# Revit family: ВЦН_ЕС_Eng
name_source: partatom
category: Mechanical Equipment
units: mm (PartAtom-declared; Revit-internal decimal feet)

## family parameters
Always vertical = Yes
Classification = None
Cut with Voids When Loaded = No
Part Type = Normal
Room Calculation Point = No
Round Connector Dimension = Use Diameter
Shared = No
Work Plane-Based = No

## types (16) — shared parameters
00_20_Manufacturer = Vents
00_20_Name = Exhaust centrifugal fan
Casing Material = Metal, painted, blue, matte RAL 5007
Description = External wall mounting
Frequency = 50 Hz
Load Classification = HVAC
Maintenance zone material = <By Category>
Manufacturer = Vents
Number of Fase = 1
URL = https://ventilation-system.com
Voltage = 230 V
zero-valued in all types: Default Elevation

## per-type parameters (varying)
- VCN 100: Amperage=0 A; Apparent Load=71 VA; B=260 mm  [stored 0.853018 ft]; B1=256 mm  [stored 0.839895 ft]; D=100 mm  [stored 0.328084 ft]; Diameter=100 mm  [stored 0.328084 ft]; H=355 mm; Height=355 mm; Horizon=9; L=138 mm  [stored 0.452756 ft]; L1=46 mm  [stored 0.150919 ft]; L2=92 mm  [stored 0.301837 ft]; Length=260 mm  [stored 0.853018 ft]; Maximum Air Flow=325.0 m³/h; Power=71 W; R=50 mm  [stored 0.164042 ft]; R1=65 mm; R3=52 mm  [stored 0.170604 ft]; Sound pressure level at 3 m distance=54 dBA; Temperature of moving air=55 °C; Vertical=10; Weight=3.82 kg; Width=138 mm  [stored 0.452756 ft]; b1=128 mm  [stored 0.419948 ft]; h=178 mm  [stored 0.58399 ft]
- VCN 200: Amperage=0 A; Apparent Load=97 VA; B=300 mm; B1=296 mm; D=200 mm; Diameter=200 mm; H=400 mm; Height=400 mm; Horizon=9; L=138 mm  [stored 0.452756 ft]; L1=46 mm  [stored 0.150919 ft]; L2=92 mm  [stored 0.301837 ft]; Length=300 mm; Maximum Air Flow=700.0 m³/h; Power=96 W; R=100 mm  [stored 0.328084 ft]; R1=130 mm  [stored 0.426509 ft]; R3=102 mm; Sound pressure level at 3 m distance=62 dBA; Temperature of moving air=55 °C; Vertical=11; Weight=4.62 kg; Width=138 mm  [stored 0.452756 ft]; b1=148 mm; h=200 mm
- VCN 125: Amperage=0 A; Apparent Load=76 VA; B=260 mm  [stored 0.853018 ft]; B1=256 mm  [stored 0.839895 ft]; D=125 mm; Diameter=125 mm; H=355 mm; Height=355 mm; Horizon=9; L=138 mm  [stored 0.452756 ft]; L1=46 mm  [stored 0.150919 ft]; L2=92 mm  [stored 0.301837 ft]; Length=260 mm  [stored 0.853018 ft]; Maximum Air Flow=485.0 m³/h; Power=75 W; R=63 mm; R1=81 mm; R3=64 mm  [stored 0.209974 ft]; Sound pressure level at 3 m distance=54 dBA; Temperature of moving air=55 °C; Vertical=10; Weight=3.82 kg; Width=138 mm  [stored 0.452756 ft]; b1=128 mm  [stored 0.419948 ft]; h=178 mm  [stored 0.58399 ft]
- VCN 150: Amperage=0 A; Apparent Load=97 VA; B=300 mm; B1=296 mm; D=150 mm; Diameter=150 mm; H=400 mm; Height=400 mm; Horizon=9; L=138 mm  [stored 0.452756 ft]; L1=46 mm  [stored 0.150919 ft]; L2=92 mm  [stored 0.301837 ft]; Length=300 mm; Maximum Air Flow=630.0 m³/h; Power=96 W; R=75 mm; R1=98 mm  [stored 0.321522 ft]; R3=77 mm  [stored 0.252625 ft]; Sound pressure level at 3 m distance=58 dBA; Temperature of moving air=55 °C; Vertical=11; Weight=4.53 kg; Width=138 mm  [stored 0.452756 ft]; b1=148 mm; h=200 mm
- VCN 160: Amperage=0 A; Apparent Load=94 VA; B=300 mm; B1=296 mm; D=160 mm; Diameter=160 mm; H=400 mm; Height=400 mm; Horizon=9; L=138 mm  [stored 0.452756 ft]; L1=46 mm  [stored 0.150919 ft]; L2=92 mm  [stored 0.301837 ft]; Length=300 mm; Maximum Air Flow=650.0 m³/h; Power=95 W; R=80 mm  [stored 0.262467 ft]; R1=104 mm; R3=82 mm; Sound pressure level at 3 m distance=60 dBA; Temperature of moving air=55 °C; Vertical=11; Weight=4.53 kg; Width=138 mm  [stored 0.452756 ft]; b1=148 mm; h=200 mm
- VCN 200 К: Amperage=0 A; Apparent Load=97 VA; B=300 mm; B1=296 mm; D=200 mm; Diameter=200 mm; H=400 mm; Height=400 mm; Horizon=9; L=138 mm  [stored 0.452756 ft]; L1=46 mm  [stored 0.150919 ft]; L2=92 mm  [stored 0.301837 ft]; Length=300 mm; Maximum Air Flow=640.0 m³/h; Power=96 W; R=100 mm  [stored 0.328084 ft]; R1=130 mm  [stored 0.426509 ft]; R3=102 mm; Sound pressure level at 3 m distance=62 dBA; Temperature of moving air=55 °C; Vertical=11; Weight=4.62 kg; Width=138 mm  [stored 0.452756 ft]; b1=148 mm; h=200 mm
- VCN 160 К: Amperage=0 A; Apparent Load=94 VA; B=300 mm; B1=296 mm; D=160 mm; Diameter=160 mm; H=400 mm; Height=400 mm; Horizon=9; L=138 mm  [stored 0.452756 ft]; L1=46 mm  [stored 0.150919 ft]; L2=92 mm  [stored 0.301837 ft]; Length=300 mm; Maximum Air Flow=590.0 m³/h; Power=95 W; R=80 mm  [stored 0.262467 ft]; R1=104 mm; R3=82 mm; Sound pressure level at 3 m distance=60 dBA; Temperature of moving air=55 °C; Vertical=11; Weight=4.53 kg; Width=138 mm  [stored 0.452756 ft]; b1=148 mm; h=200 mm
- VCN 150 К: Amperage=0 A; Apparent Load=97 VA; B=300 mm; B1=296 mm; D=150 mm; Diameter=150 mm; H=400 mm; Height=400 mm; Horizon=9; L=138 mm  [stored 0.452756 ft]; L1=46 mm  [stored 0.150919 ft]; L2=92 mm  [stored 0.301837 ft]; Length=300 mm; Maximum Air Flow=565.0 m³/h; Power=96 W; R=75 mm; R1=98 mm  [stored 0.321522 ft]; R3=77 mm  [stored 0.252625 ft]; Sound pressure level at 3 m distance=58 dBA; Temperature of moving air=55 °C; Vertical=11; Weight=4.53 kg; Width=138 mm  [stored 0.452756 ft]; b1=148 mm; h=200 mm
- VCN 125 К: Amperage=0 A; Apparent Load=76 VA; B=260 mm  [stored 0.853018 ft]; B1=256 mm  [stored 0.839895 ft]; D=125 mm; Diameter=125 mm; H=355 mm; Height=355 mm; Horizon=9; L=138 mm  [stored 0.452756 ft]; L1=46 mm  [stored 0.150919 ft]; L2=92 mm  [stored 0.301837 ft]; Length=260 mm  [stored 0.853018 ft]; Maximum Air Flow=450.0 m³/h; Power=75 W; R=63 mm; R1=81 mm; R3=64 mm  [stored 0.209974 ft]; Sound pressure level at 3 m distance=54 dBA; Temperature of moving air=55 °C; Vertical=10; Weight=3.82 kg; Width=138 mm  [stored 0.452756 ft]; b1=128 mm  [stored 0.419948 ft]; h=178 mm  [stored 0.58399 ft]
- VCN 100 К: Amperage=0 A; Apparent Load=71 VA; B=260 mm  [stored 0.853018 ft]; B1=256 mm  [stored 0.839895 ft]; D=100 mm  [stored 0.328084 ft]; Diameter=100 mm  [stored 0.328084 ft]; H=355 mm; Height=355 mm; Horizon=9; L=138 mm  [stored 0.452756 ft]; L1=46 mm  [stored 0.150919 ft]; L2=92 mm  [stored 0.301837 ft]; Length=260 mm  [stored 0.853018 ft]; Maximum Air Flow=295.0 m³/h; Power=71 W; R=50 mm  [stored 0.164042 ft]; R1=65 mm; R3=52 mm  [stored 0.170604 ft]; Sound pressure level at 3 m distance=54 dBA; Temperature of moving air=55 °C; Vertical=10; Weight=3.82 kg; Width=138 mm  [stored 0.452756 ft]; b1=128 mm  [stored 0.419948 ft]; h=178 mm  [stored 0.58399 ft]
- VCN 100 EC: Amperage=1 A; Apparent Load=122 VA; B=260 mm  [stored 0.853018 ft]; B1=256 mm  [stored 0.839895 ft]; D=100 mm  [stored 0.328084 ft]; Diameter=100 mm  [stored 0.328084 ft]; H=355 mm; Height=355 mm; Horizon=9; L=140 mm  [stored 0.459318 ft]; L1=47 mm; L2=93 mm; Length=260 mm  [stored 0.853018 ft]; Maximum Air Flow=313.0 m³/h; Power=89 W; R=50 mm  [stored 0.164042 ft]; R1=65 mm; R3=52 mm  [stored 0.170604 ft]; Sound pressure level at 3 m distance=55 dBA; Temperature of moving air=-25...+40 °C; Vertical=10; Weight=3.60 kg; Width=140 mm  [stored 0.459318 ft]; b1=128 mm  [stored 0.419948 ft]; h=178 mm  [stored 0.58399 ft]
- VCN 125 ЕС: Amperage=1 A; Apparent Load=191 VA; B=260 mm  [stored 0.853018 ft]; B1=256 mm  [stored 0.839895 ft]; D=125 mm; Diameter=125 mm; H=355 mm; Height=355 mm; Horizon=9; L=140 mm  [stored 0.459318 ft]; L1=47 mm; L2=93 mm; Length=260 mm  [stored 0.853018 ft]; Maximum Air Flow=480.0 m³/h; Power=103 W; R=63 mm; R1=81 mm; R3=64 mm  [stored 0.209974 ft]; Sound pressure level at 3 m distance=57 dBA; Temperature of moving air=-25...+40 °C; Vertical=10; Weight=3.60 kg; Width=140 mm  [stored 0.459318 ft]; b1=128 mm  [stored 0.419948 ft]; h=178 mm  [stored 0.58399 ft]
- VCN 150 ЕС: Amperage=1 A; Apparent Load=173 VA; B=300 mm; B1=296 mm; D=150 mm; Diameter=150 mm; H=400 mm; Height=400 mm; Horizon=9; L=140 mm  [stored 0.459318 ft]; L1=47 mm; L2=93 mm; Length=300 mm; Maximum Air Flow=550.0 m³/h; Power=92 W; R=75 mm; R1=98 mm  [stored 0.321522 ft]; R3=77 mm  [stored 0.252625 ft]; Sound pressure level at 3 m distance=56 dBA; Temperature of moving air=-25...+40 °C; Vertical=11; Weight=4.70 kg; Width=140 mm  [stored 0.459318 ft]; b1=148 mm; h=200 mm
- VCN 160 ЕС: Amperage=1 A; Apparent Load=173 VA; B=300 mm; B1=296 mm; D=160 mm; Diameter=160 mm; H=400 mm; Height=400 mm; Horizon=9; L=140 mm  [stored 0.459318 ft]; L1=47 mm; L2=93 mm; Length=300 mm; Maximum Air Flow=585.0 m³/h; Power=92 W; R=80 mm  [stored 0.262467 ft]; R1=104 mm; R3=82 mm; Sound pressure level at 3 m distance=55 dBA; Temperature of moving air=-25...+40 °C; Vertical=11; Weight=4.70 kg; Width=140 mm  [stored 0.459318 ft]; b1=148 mm; h=200 mm
- VCN 200 ЕС: Amperage=1 A; Apparent Load=154 VA; B=300 mm; B1=296 mm; D=200 mm; Diameter=200 mm; H=400 mm; Height=400 mm; Horizon=9; L=140 mm  [stored 0.459318 ft]; L1=47 mm; L2=93 mm; Length=300 mm; Maximum Air Flow=535.0 m³/h; Power=79 W; R=100 mm  [stored 0.328084 ft]; R1=130 mm  [stored 0.426509 ft]; R3=102 mm; Sound pressure level at 3 m distance=55 dBA; Temperature of moving air=-25...+40 °C; Vertical=11; Weight=4.70 kg; Width=140 mm  [stored 0.459318 ft]; b1=148 mm; h=200 mm
- VCN 200 ЕС S: Amperage=1 A; Apparent Load=198 VA; B=325 mm; B1=321 mm; D=200 mm; Diameter=200 mm; H=400 mm; Height=400 mm; Horizon=8; L=181 mm; L1=60 mm  [stored 0.19685 ft]; L2=121 mm; Length=325 mm; Maximum Air Flow=755.0 m³/h; Power=102 W; R=100 mm  [stored 0.328084 ft]; R1=130 mm  [stored 0.426509 ft]; R3=102 mm; Sound pressure level at 3 m distance=58 dBA; Temperature of moving air=-25...+40 °C; Vertical=12; Weight=5.30 kg; Width=181 mm; b1=161 mm; h=200 mm

note: column(s) folded — value = type name in every type: 00_20_Type

note: [stored X ft] marks values corroborated as IEEE doubles in the binary element streams (Revit-internal decimal feet)
